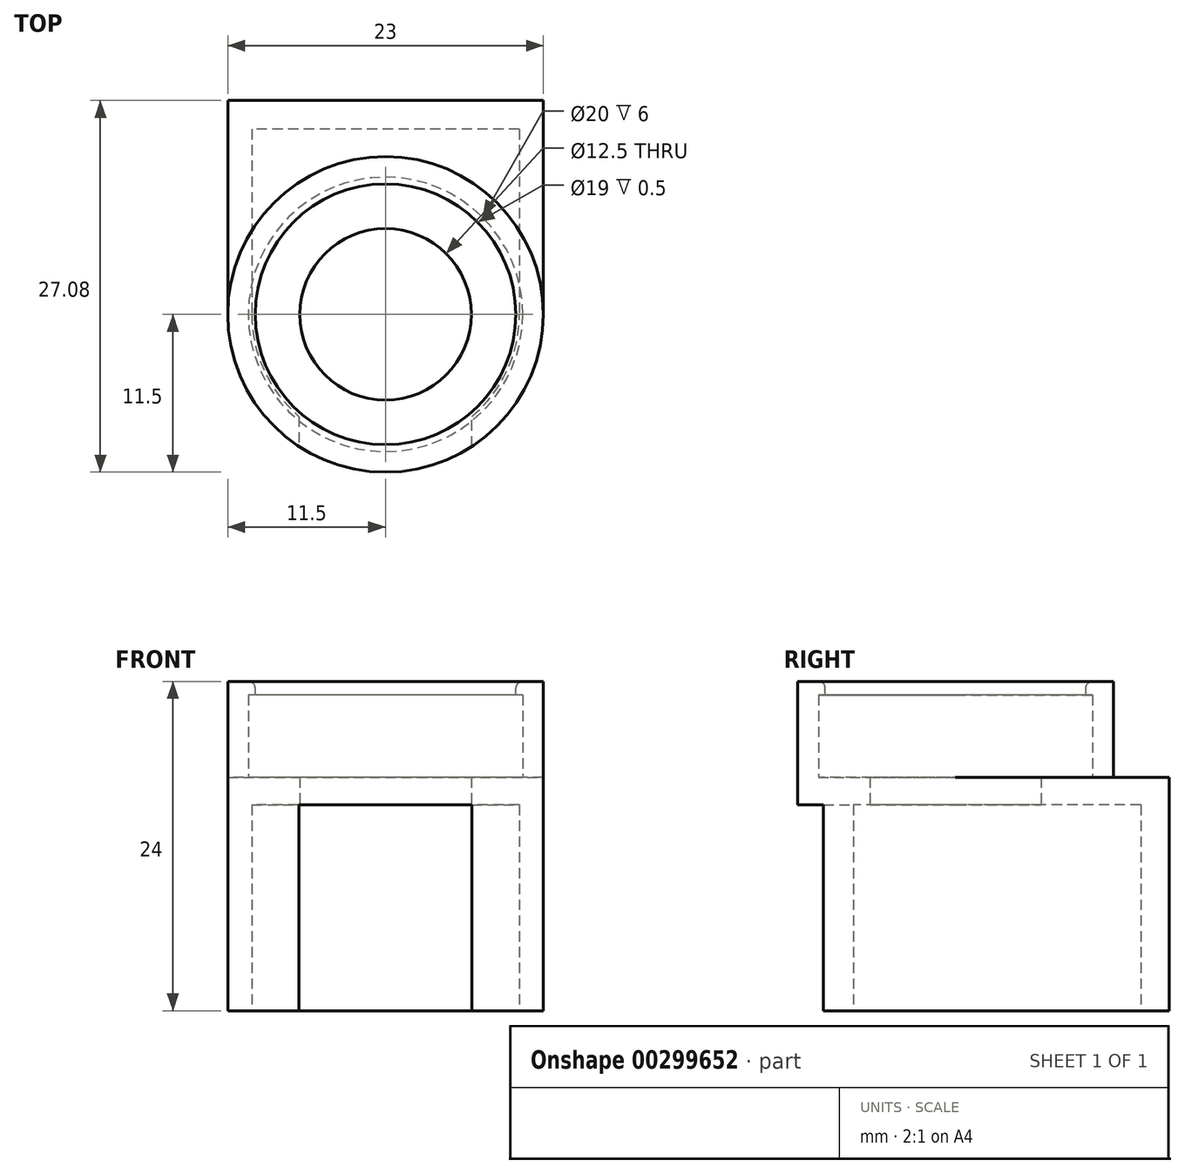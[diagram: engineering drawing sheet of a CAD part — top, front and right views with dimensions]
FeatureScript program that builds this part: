
annotation { "Feature Type Name" : "Feature", "Feature Type Description" : "" }
export const myFeature = defineFeature(function(context is Context, id is Id, definition is map)
    precondition{}
    {
        {
            var Q0;
            Q0=qCreatedBy(makeId("Top.planeOp"),FACE);
            var sketch = newSketch(context, id + "F0", { "sketchPlane" : qUnion([Q0])});
            skCircle(sketch, "E0", {"center": v(0, 0) * mm, "radius": 9.75 * mm});
            skCircle(sketch, "E1", {"center": v(0, 0) * mm, "radius": 11.5 * mm});
            skLineSegment(sketch, "E2", {"start": v(-9.75, 13.5) * mm, "end": v(-9.75, 0) * mm});
            skLineSegment(sketch, "E3", {"start": v(9.75, 13.5) * mm, "end": v(9.75, 0) * mm});
            skLineSegment(sketch, "E4", {"start": v(-11.5, 0) * mm, "end": v(-11.5, 13.5) * mm});
            skLineSegment(sketch, "E5", {"start": v(11.5, 0) * mm, "end": v(11.5, 13.5) * mm});
            skLineSegment(sketch, "E6", {"start": v(11.5, 13.5) * mm, "end": v(-11.5, 13.5) * mm});
            skLineSegment(sketch, "E7", {"start": v(-11.5, 13.5) * mm, "end": v(-11.5, 15.58) * mm});
            skLineSegment(sketch, "E8", {"start": v(11.5, 15.58) * mm, "end": v(11.5, 13.5) * mm});
            skLineSegment(sketch, "E9", {"start": v(-11.5, 0) * mm, "end": v(11.5, 0) * mm});
            skLineSegment(sketch, "E10", {"start": v(-9.75, 0) * mm, "end": v(-6.3, 0) * mm});
            skLineSegment(sketch, "E11", {"start": v(9.75, 0) * mm, "end": v(6.3, 0) * mm});
            skLineSegment(sketch, "E12", {"start": v(-6.3, 0) * mm, "end": v(-6.3, -15.44) * mm});
            skLineSegment(sketch, "E13", {"start": v(-6.3, -15.44) * mm, "end": v(6.3, -15.44) * mm});
            skLineSegment(sketch, "E14", {"start": v(6.3, -15.44) * mm, "end": v(6.3, 0) * mm});
            skLineSegment(sketch, "E15", {"start": v(-11.5, 15.58) * mm, "end": v(11.5, 15.58) * mm});
            skPoint(sketch, "E16.orphan", {"position": v(11.5, 21.03) * mm});
            skSolve(sketch);
        }
        {
            var Q0;
            {var subQ3=sQuery(id+"F0.wireOp",EDGE,"E12");var subQ5=sQuery(id+"F0.wireOp",EDGE,"E1");var subQ7=makeQuery(id+"F0.imprint","INTERSECT",VERTEX,{"derivedFrom":[subQ5,subQ3]});Q0=makeQuery(id+"F0.imprint","IMPRINT",FACE,{"disambiguationData":[TD([[makeQuery(id+"F0.imprint","IMPRINT",EDGE,{"disambiguationData":[TD([[subQ7,1.0]])],"derivedFrom":subQ3}),-1.0]])]});}
            var Q1;
            {var subQ3=sQuery(id+"F0.wireOp",EDGE,"E14");var subQ5=sQuery(id+"F0.wireOp",EDGE,"E1");var subQ7=makeQuery(id+"F0.imprint","INTERSECT",VERTEX,{"derivedFrom":[subQ5,subQ3]});Q1=makeQuery(id+"F0.imprint","IMPRINT",FACE,{"disambiguationData":[TD([[makeQuery(id+"F0.imprint","IMPRINT",EDGE,{"disambiguationData":[TD([[subQ7,-1.0]])],"derivedFrom":subQ3}),-1.0]])]});}
            var Q2;
            {var subQ0=sQuery(id+"F0.wireOp",EDGE,"E5");Q2=makeQuery(id+"F0.imprint","IMPRINT",FACE,{"disambiguationData":[TD([[makeQuery(id+"F0.imprint","IMPRINT",EDGE,{"derivedFrom":subQ0}),1.0]])]});}
            var Q3;
            {var subQ1=sQuery(id+"F0.wireOp",EDGE,"E1");var subQ3=sQuery(id+"F0.wireOp",EDGE,"E3");var subQ4=makeQuery(id+"F0.imprint","INTERSECT",VERTEX,{"derivedFrom":[subQ1,subQ3]});Q3=makeQuery(id+"F0.imprint","IMPRINT",FACE,{"disambiguationData":[TD([[makeQuery(id+"F0.imprint","IMPRINT",EDGE,{"disambiguationData":[TD([[subQ4,1.0]])],"derivedFrom":subQ1}),1.0]])]});}
            var Q4;
            {var subQ0=sQuery(id+"F0.wireOp",EDGE,"E4");Q4=makeQuery(id+"F0.imprint","IMPRINT",FACE,{"disambiguationData":[TD([[makeQuery(id+"F0.imprint","IMPRINT",EDGE,{"derivedFrom":subQ0}),-1.0]])]});}
            var Q5;
            {var subQ1=sQuery(id+"F0.wireOp",EDGE,"E1");var subQ3=sQuery(id+"F0.wireOp",EDGE,"E2");var subQ4=makeQuery(id+"F0.imprint","INTERSECT",VERTEX,{"derivedFrom":[subQ1,subQ3]});Q5=makeQuery(id+"F0.imprint","IMPRINT",FACE,{"disambiguationData":[TD([[makeQuery(id+"F0.imprint","IMPRINT",EDGE,{"disambiguationData":[TD([[subQ4,-1.0]])],"derivedFrom":subQ1}),1.0]])]});}
            var Q6;
            {var subQ0=sQuery(id+"F0.wireOp",EDGE,"E7");Q6=makeQuery(id+"F0.imprint","IMPRINT",FACE,{"disambiguationData":[TD([[makeQuery(id+"F0.imprint","IMPRINT",EDGE,{"derivedFrom":subQ0}),-1.0]])]});}
            extrude(context, id + "F1", {"entities" : qUnion([Q0, Q1, Q2, Q3, Q4, Q5, Q6]), "depth" : 15 * mm});
        }
        {
            var Q0;
            Q0=makeQuery(id+"F1.opExtrude","CAP_FACE",FACE,{"disambiguationData":[OSD([sQuery(id+"F0.wireOp",EDGE,"E0"),sQuery(id+"F0.wireOp",EDGE,"E1"),sQuery(id+"F0.wireOp",EDGE,"E2"),sQuery(id+"F0.wireOp",EDGE,"E3"),sQuery(id+"F0.wireOp",EDGE,"E4"),sQuery(id+"F0.wireOp",EDGE,"E5"),sQuery(id+"F0.wireOp",EDGE,"E6"),sQuery(id+"F0.wireOp",EDGE,"E7"),sQuery(id+"F0.wireOp",EDGE,"JEOptelM-5wX6-nScR-b6Dc-lIi6HULPdI30"),sQuery(id+"F0.wireOp",EDGE,"E8"),sQuery(id+"F0.wireOp",EDGE,"E12"),sQuery(id+"F0.wireOp",EDGE,"E14")])],"isStart":false});
            var sketch = newSketch(context, id + "F2", { "sketchPlane" : qUnion([Q0])});
            skLineSegment(sketch, "E17", {"start": v(-11.5, 15.58) * mm, "end": v(-11.5, 0) * mm});
            skLineSegment(sketch, "E18", {"start": v(-11.5, 0) * mm, "end": v(11.5, 0) * mm});
            skLineSegment(sketch, "E19", {"start": v(11.5, 0) * mm, "end": v(11.5, 15.58) * mm});
            skLineSegment(sketch, "E20", {"start": v(11.5, 15.58) * mm, "end": v(-11.5, 15.58) * mm});
            skCircle(sketch, "E21", {"center": v(0, 0) * mm, "radius": 11.5 * mm});
            skCircle(sketch, "E22", {"center": v(0, 0) * mm, "radius": 6.25 * mm});
            skSolve(sketch);
        }
        {
            var Q0;
            Q0 = qSketchRegion(id + "F2", true);
            extrude(context, id + "F3", {"entities" : qUnion([Q0]), "operationType" : NewBodyOperationType.ADD, "depth" : 2 * mm});
        }
        {
            var Q0;
            Q0=makeQuery(id+"F3.opExtrude","CAP_FACE",FACE,{"disambiguationData":[OSD([sQuery(id+"F2.wireOp",EDGE,"E17"),sQuery(id+"F2.wireOp",EDGE,"E19"),sQuery(id+"F2.wireOp",EDGE,"E20"),sQuery(id+"F2.wireOp",EDGE,"E21")])],"isStart":false});
            var sketch = newSketch(context, id + "F4", { "sketchPlane" : qUnion([Q0])});
            skCircle(sketch, "E23", {"center": v(0, 0) * mm, "radius": 10 * mm});
            skCircle(sketch, "E24", {"center": v(0, 0) * mm, "radius": 11.5 * mm});
            skSolve(sketch);
        }
        {
            var Q0;
            Q0 = qSketchRegion(id + "F4", true);
            extrude(context, id + "F5", {"entities" : qUnion([Q0]), "operationType" : NewBodyOperationType.ADD, "depth" : 7 * mm});
        }
        {
            var Q0;
            Q0=makeQuery(id+"F5.opExtrude","CAP_FACE",FACE,{"disambiguationData":[OSD([sQuery(id+"F4.wireOp",EDGE,"E23"),sQuery(id+"F4.wireOp",EDGE,"E24")])],"isStart":false});
            var sketch = newSketch(context, id + "F6", { "sketchPlane" : qUnion([Q0])});
            skCircle(sketch, "E25", {"center": v(0, 0) * mm, "radius": 11.5 * mm});
            skCircle(sketch, "E26", {"center": v(0, 0) * mm, "radius": 9.5 * mm});
            skSolve(sketch);
        }
        {
            var Q0;
            Q0 = qSketchRegion(id + "F6", true);
            extrude(context, id + "F7", {"entities" : qUnion([Q0]), "operationType" : NewBodyOperationType.ADD, "oppositeDirection" : true, "depth" : 1 * mm});
        }
        {
            var Q0;
            Q0=makeQuery(id+"F7.opExtrude","CAP_EDGE",EDGE,{"disambiguationData":[OSD([sQuery(id+"F6.wireOp",EDGE,"E26")])],"isStart":true});
            fillet(context, id + "F8", {"entities" : qUnion([Q0]), "radius" : 0.5 * mm, "tangentPropagation" : true, "allowEdgeOverflow" : false});
        }
    });
